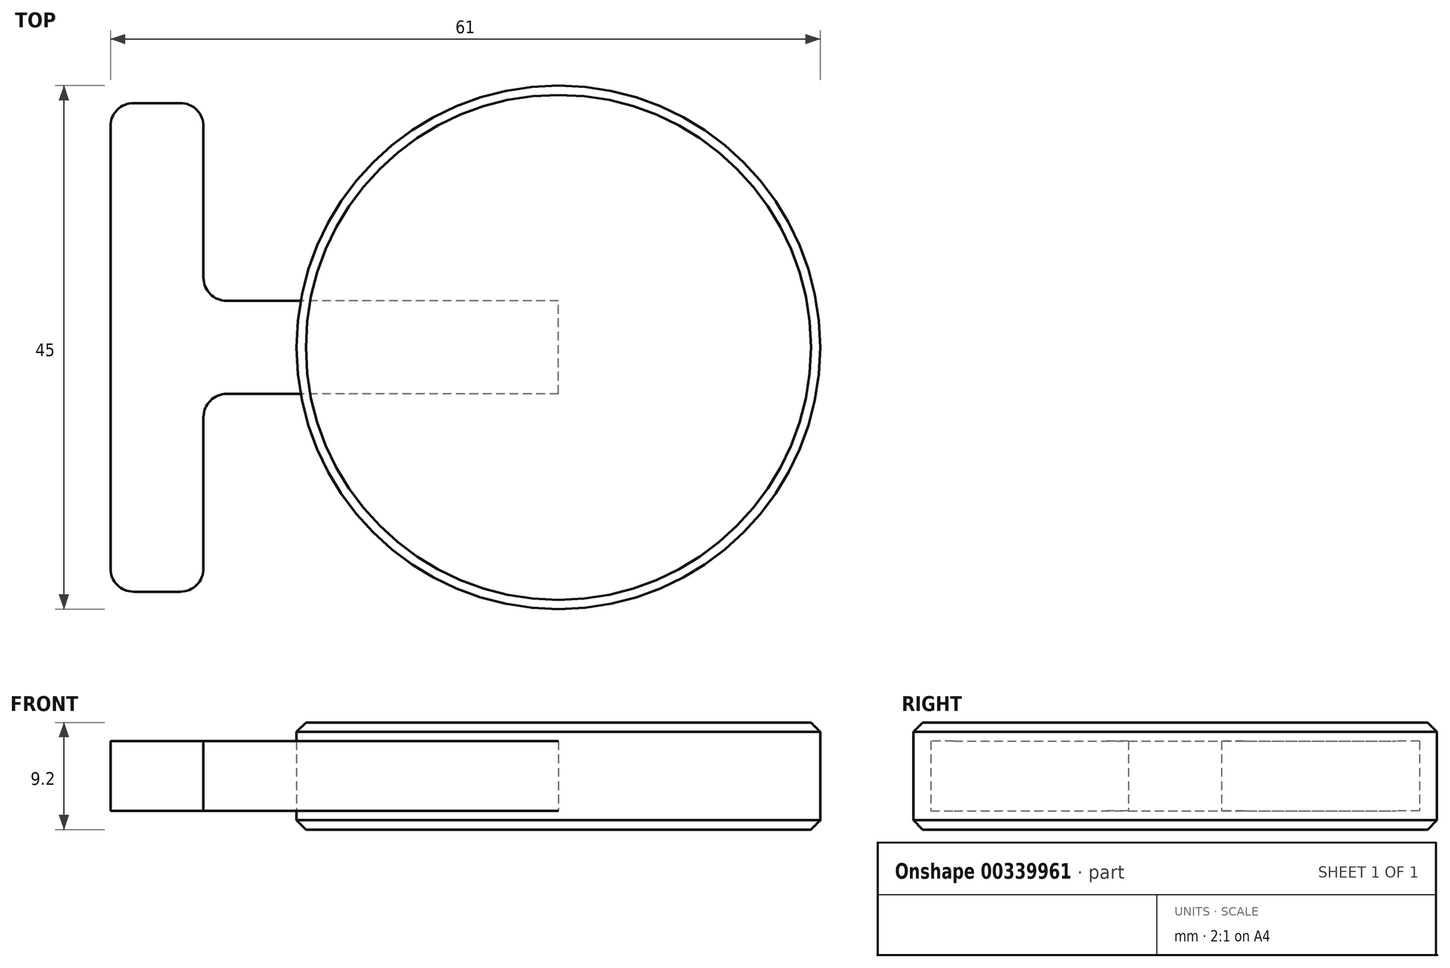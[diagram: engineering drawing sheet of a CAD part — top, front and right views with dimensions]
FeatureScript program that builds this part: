
annotation { "Feature Type Name" : "Feature", "Feature Type Description" : "" }
export const myFeature = defineFeature(function(context is Context, id is Id, definition is map)
    precondition{}
    {
        {
            var Q0;
            Q0=qCreatedBy(makeId("Top.planeOp"),FACE);
            var sketch = newSketch(context, id + "F0", { "sketchPlane" : qUnion([Q0])});
            skCircle(sketch, "E0", {"center": v(0, 0) * mm, "radius": 22.5 * mm});
            skSolve(sketch);
        }
        {
            var Q0;
            Q0 = qSketchRegion(id + "F0", true);
            extrude(context, id + "F1", {"entities" : qUnion([Q0]), "depth" : 4.6 * mm, "offsetDistance" : 25 * mm, "hasSecondDirection" : true, "secondDirectionOppositeDirection" : true, "secondDirectionDepth" : 4.6 * mm});
        }
        {
            var Q0;
            Q0=qCreatedBy(makeId("Top.planeOp"),FACE);
            var sketch = newSketch(context, id + "F2", { "sketchPlane" : qUnion([Q0])});
            skLineSegment(sketch, "E1.bottom", {"start": v(0, -4) * mm, "end": v(-34.5, -4) * mm});
            skLineSegment(sketch, "E1.top", {"start": v(0, 4) * mm, "end": v(-34.5, 4) * mm});
            skLineSegment(sketch, "E1.left", {"start": v(0, -4) * mm, "end": v(0, 4) * mm});
            skLineSegment(sketch, "E1.right", {"start": v(-34.5, -4) * mm, "end": v(-34.5, 4) * mm});
            skPoint(sketch, "E1.middle", {"position": v(-17.25, 0) * mm});
            skLineSegment(sketch, "E2.bottom", {"start": v(-30.5, -21) * mm, "end": v(-38.5, -21) * mm});
            skLineSegment(sketch, "E2.top", {"start": v(-30.5, 21) * mm, "end": v(-38.5, 21) * mm});
            skLineSegment(sketch, "E2.left", {"start": v(-30.5, -21) * mm, "end": v(-30.5, 21) * mm});
            skLineSegment(sketch, "E2.right", {"start": v(-38.5, -21) * mm, "end": v(-38.5, 21) * mm});
            skPoint(sketch, "E2.middle", {"position": v(-34.5, 0) * mm});
            skSolve(sketch);
        }
        {
            var Q0;
            Q0 = qSketchRegion(id + "F2", true);
            extrude(context, id + "F3", {"entities" : qUnion([Q0]), "depth" : 3 * mm, "offsetDistance" : 25 * mm, "hasSecondDirection" : true, "secondDirectionOppositeDirection" : true, "secondDirectionDepth" : 3 * mm});
        }
        {
            var Q0;
            Q0=makeQuery(id+"F1.opExtrude","CAP_EDGE",EDGE,{"disambiguationData":[OSD([sQuery(id+"F0.wireOp",EDGE,"E0")])],"isStart":false});
            var Q1;
            Q1=makeQuery(id+"F1.opExtrude","CAP_EDGE",EDGE,{"disambiguationData":[OSD([sQuery(id+"F0.wireOp",EDGE,"E0")])],"isStart":true});
            chamfer(context, id + "F4", {"entities" : qUnion([Q0, Q1]), "width" : 0.8 * mm, "tangentPropagation" : true});
        }
        {
            var Q0;
            Q0=makeQuery(id+"F3.opExtrude","SWEPT_EDGE",EDGE,{"disambiguationData":[OSD([sQuery(id+"F2.wireOp",EDGE,"E1.bottom"),sQuery(id+"F2.wireOp",EDGE,"E2.left")])]});
            var Q1;
            Q1=makeQuery(id+"F3.opExtrude","SWEPT_EDGE",EDGE,{"disambiguationData":[OSD([sQuery(id+"F2.wireOp",EDGE,"E1.top"),sQuery(id+"F2.wireOp",EDGE,"E2.left")])]});
            fillet(context, id + "F5", {"entities" : qUnion([Q0, Q1]), "radius" : 2 * mm, "tangentPropagation" : true, "allowEdgeOverflow" : false});
        }
        {
            var Q0;
            Q0=makeQuery(id+"F3.opExtrude","SWEPT_EDGE",EDGE,{"disambiguationData":[OSD([sQuery(id+"F2.wireOp",EDGE,"E2.bottom"),sQuery(id+"F2.wireOp",EDGE,"E2.left")])]});
            var Q1;
            Q1=makeQuery(id+"F3.opExtrude","SWEPT_EDGE",EDGE,{"disambiguationData":[OSD([sQuery(id+"F2.wireOp",EDGE,"E2.bottom"),sQuery(id+"F2.wireOp",EDGE,"E2.right")])]});
            var Q2;
            Q2=makeQuery(id+"F3.opExtrude","SWEPT_EDGE",EDGE,{"disambiguationData":[OSD([sQuery(id+"F2.wireOp",EDGE,"E2.top"),sQuery(id+"F2.wireOp",EDGE,"E2.left")])]});
            var Q3;
            Q3=makeQuery(id+"F3.opExtrude","SWEPT_EDGE",EDGE,{"disambiguationData":[OSD([sQuery(id+"F2.wireOp",EDGE,"E2.top"),sQuery(id+"F2.wireOp",EDGE,"E2.right")])]});
            fillet(context, id + "F6", {"entities" : qUnion([Q0, Q1, Q2, Q3]), "radius" : 2 * mm, "tangentPropagation" : true, "allowEdgeOverflow" : false});
        }
    });
